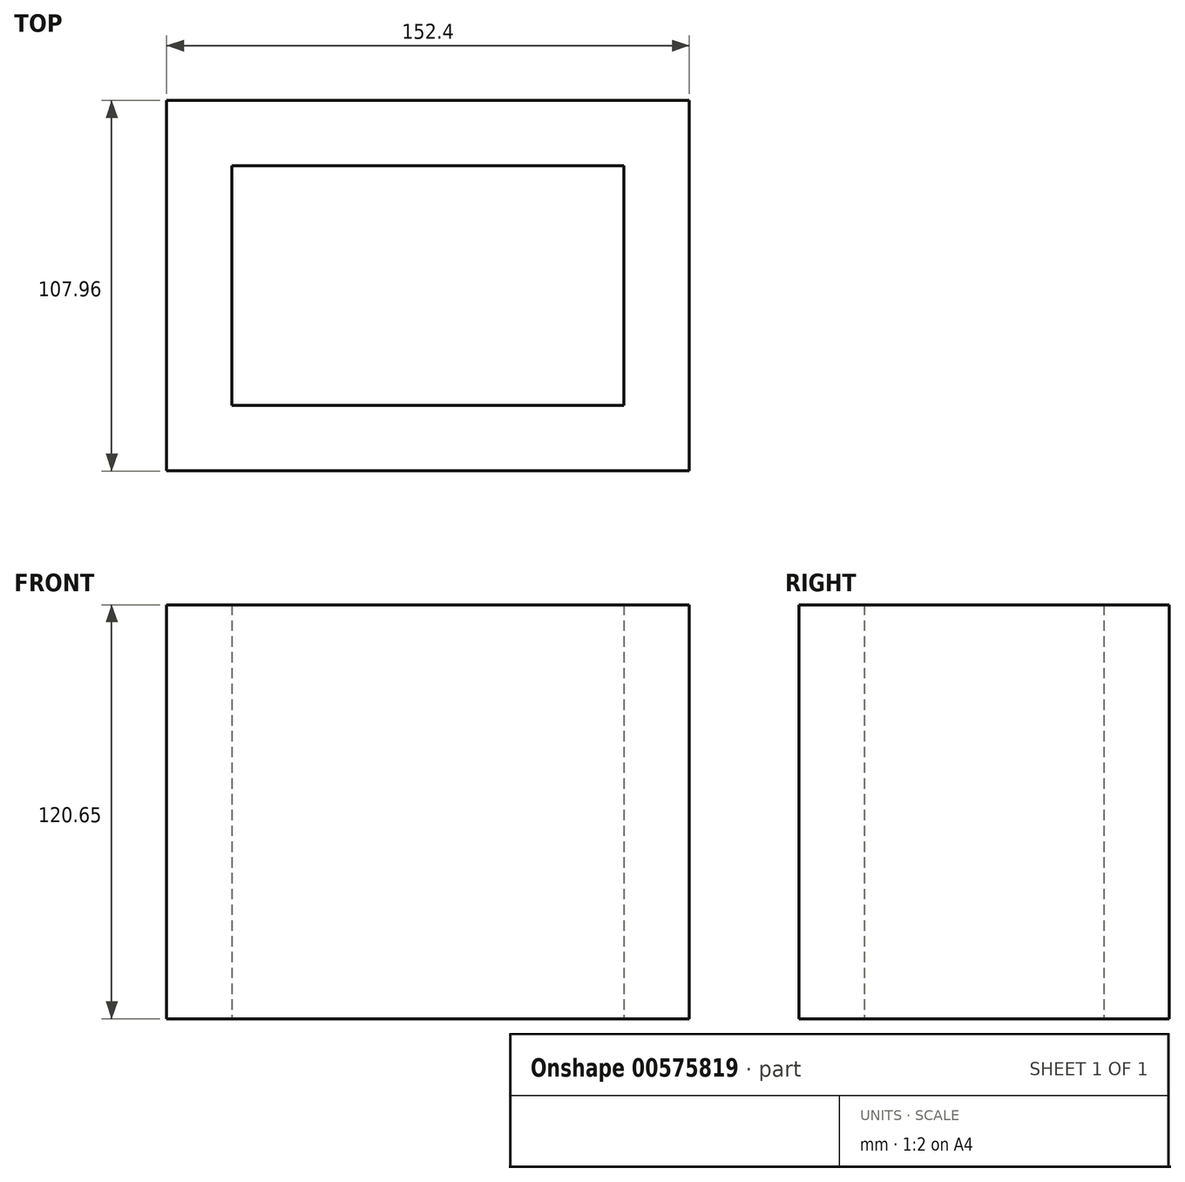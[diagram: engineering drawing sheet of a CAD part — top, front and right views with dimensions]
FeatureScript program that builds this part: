
annotation { "Feature Type Name" : "Feature", "Feature Type Description" : "" }
export const myFeature = defineFeature(function(context is Context, id is Id, definition is map)
    precondition{}
    {
        {
            var Q0;
            Q0=qCreatedBy(makeId("Top.planeOp"),FACE);
            var sketch = newSketch(context, id + "F0", { "sketchPlane" : qUnion([Q0])});
            skLineSegment(sketch, "E0.bottom", {"start": v(57.15, 34.93) * mm, "end": v(-57.15, 34.93) * mm});
            skLineSegment(sketch, "E0.top", {"start": v(57.15, -34.92) * mm, "end": v(-57.15, -34.93) * mm});
            skLineSegment(sketch, "E0.left", {"start": v(57.15, 34.92) * mm, "end": v(57.15, -34.93) * mm});
            skLineSegment(sketch, "E0.right", {"start": v(-57.15, 34.93) * mm, "end": v(-57.15, -34.92) * mm});
            skPoint(sketch, "E0.middle", {"position": v(0, 0) * mm});
            skLineSegment(sketch, "E1.bottom", {"start": v(76.2, 53.98) * mm, "end": v(-76.2, 53.97) * mm});
            skLineSegment(sketch, "E1.top", {"start": v(76.2, -53.98) * mm, "end": v(-76.2, -53.98) * mm});
            skLineSegment(sketch, "E1.left", {"start": v(76.2, 53.98) * mm, "end": v(76.2, -53.97) * mm});
            skLineSegment(sketch, "E1.right", {"start": v(-76.2, 53.97) * mm, "end": v(-76.2, -53.98) * mm});
            skSolve(sketch);
        }
        {
            var Q0;
            Q0=makeQuery(id+"F0.imprint","IMPRINT",FACE,{"disambiguationData":[TD([[makeQuery(id+"F0.imprint","IMPRINT",EDGE,{"derivedFrom":sQuery(id+"F0.wireOp",EDGE,"E0.bottom")}),-1.0]])]});
            extrude(context, id + "F1", {"entities" : qUnion([Q0]), "depth" : 120.65 * mm, "offsetDistance" : 25.4 * mm});
        }
    });
